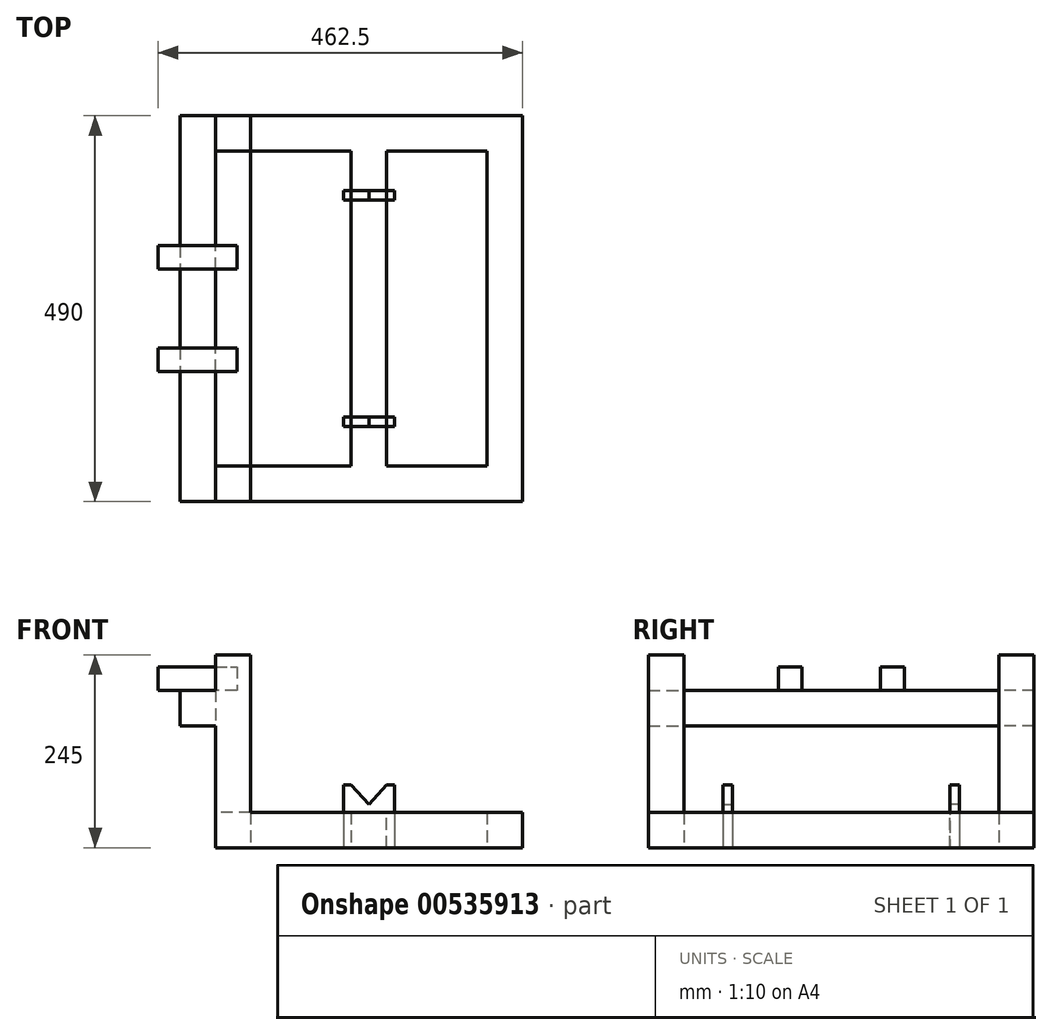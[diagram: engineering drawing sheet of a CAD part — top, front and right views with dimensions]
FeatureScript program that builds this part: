
annotation { "Feature Type Name" : "Feature", "Feature Type Description" : "" }
export const myFeature = defineFeature(function(context is Context, id is Id, definition is map)
    precondition{}
    {
        {
            var Q0;
            Q0=qCreatedBy(makeId("Top.planeOp"),FACE);
            var sketch = newSketch(context, id + "F0", { "sketchPlane" : qUnion([Q0])});
            skLineSegment(sketch, "E0.bottom", {"start": v(0, 0) * mm, "end": v(390, 0) * mm});
            skLineSegment(sketch, "E0.top", {"start": v(0, 490) * mm, "end": v(390, 490) * mm});
            skLineSegment(sketch, "E0.left", {"start": v(0, 0) * mm, "end": v(0, 490) * mm});
            skLineSegment(sketch, "E0.right", {"start": v(390, 0) * mm, "end": v(390, 490) * mm});
            skLineSegment(sketch, "E1.bottom", {"start": v(45, 445) * mm, "end": v(172.5, 445) * mm});
            skLineSegment(sketch, "E1.top", {"start": v(45, 45) * mm, "end": v(172.5, 45) * mm});
            skLineSegment(sketch, "E1.left", {"start": v(45, 445) * mm, "end": v(45, 45) * mm});
            skLineSegment(sketch, "E1.right", {"start": v(345, 445) * mm, "end": v(345, 45) * mm});
            skLineSegment(sketch, "E2", {"start": v(172.5, 445) * mm, "end": v(172.5, 45) * mm});
            skLineSegment(sketch, "E3", {"start": v(217.5, 445) * mm, "end": v(217.5, 45) * mm});
            skLineSegment(sketch, "E4.trimOffspring", {"start": v(217.5, 445) * mm, "end": v(345, 445) * mm});
            skLineSegment(sketch, "E5.trimOffspring", {"start": v(217.5, 45) * mm, "end": v(345, 45) * mm});
            skSolve(sketch);
        }
        {
            var Q0;
            Q0=makeQuery(id+"F0.imprint","IMPRINT",FACE,{"disambiguationData":[TD([[makeQuery(id+"F0.imprint","IMPRINT",EDGE,{"derivedFrom":sQuery(id+"F0.wireOp",EDGE,"E0.bottom")}),1.0]])]});
            extrude(context, id + "F1", {"entities" : qUnion([Q0]), "depth" : 45 * mm, "offsetDistance" : 25 * mm});
        }
        {
            var Q0;
            Q0=makeQuery(id+"F1.opExtrude","CAP_FACE",FACE,{"disambiguationData":[OSD([sQuery(id+"F0.wireOp",EDGE,"E0.bottom"),sQuery(id+"F0.wireOp",EDGE,"E0.top"),sQuery(id+"F0.wireOp",EDGE,"E0.left"),sQuery(id+"F0.wireOp",EDGE,"E0.right"),sQuery(id+"F0.wireOp",EDGE,"E1.bottom"),sQuery(id+"F0.wireOp",EDGE,"E1.top"),sQuery(id+"F0.wireOp",EDGE,"E1.left"),sQuery(id+"F0.wireOp",EDGE,"E1.right"),sQuery(id+"F0.wireOp",EDGE,"E2"),sQuery(id+"F0.wireOp",EDGE,"E3"),sQuery(id+"F0.wireOp",EDGE,"E4.trimOffspring"),sQuery(id+"F0.wireOp",EDGE,"E5.trimOffspring")])],"isStart":false});
            var sketch = newSketch(context, id + "F2", { "sketchPlane" : qUnion([Q0])});
            skLineSegment(sketch, "E6.bottom", {"start": v(45, 445) * mm, "end": v(0, 445) * mm});
            skLineSegment(sketch, "E6.top", {"start": v(45, 490) * mm, "end": v(0, 490) * mm});
            skLineSegment(sketch, "E6.left", {"start": v(45, 445) * mm, "end": v(45, 490) * mm});
            skLineSegment(sketch, "E6.right", {"start": v(0, 445) * mm, "end": v(0, 490) * mm});
            skLineSegment(sketch, "E7.bottom", {"start": v(45, 45) * mm, "end": v(0, 45) * mm});
            skLineSegment(sketch, "E7.top", {"start": v(45, 0) * mm, "end": v(0, 0) * mm});
            skLineSegment(sketch, "E7.left", {"start": v(45, 45) * mm, "end": v(45, 0) * mm});
            skLineSegment(sketch, "E7.right", {"start": v(0, 45) * mm, "end": v(0, 0) * mm});
            skSolve(sketch);
        }
        {
            var Q0;
            Q0=makeQuery(id+"F2.imprint","IMPRINT",FACE,{"disambiguationData":[TD([[makeQuery(id+"F2.imprint","IMPRINT",EDGE,{"derivedFrom":sQuery(id+"F2.wireOp",EDGE,"E7.bottom")}),1.0]])]});
            var Q1;
            Q1=makeQuery(id+"F2.imprint","IMPRINT",FACE,{"disambiguationData":[TD([[makeQuery(id+"F2.imprint","IMPRINT",EDGE,{"derivedFrom":sQuery(id+"F2.wireOp",EDGE,"E6.bottom")}),-1.0]])]});
            extrude(context, id + "F3", {"entities" : qUnion([Q0, Q1]), "operationType" : NewBodyOperationType.ADD, "depth" : 200 * mm, "offsetDistance" : 25 * mm});
        }
        {
            var Q0;
            Q0=makeQuery(id+"F3.boolean.opBoolean","MERGE",FACE,{"derivedFrom":[makeQuery(id+"F1.opExtrude","SWEPT_FACE",FACE,{"disambiguationData":[OSD([sQuery(id+"F0.wireOp",EDGE,"E0.left")])]}),makeQuery(id+"F3.opExtrude","SWEPT_FACE",FACE,{"disambiguationData":[OSD([sQuery(id+"F2.wireOp",EDGE,"E6.right")])]}),makeQuery(id+"F3.opExtrude","SWEPT_FACE",FACE,{"disambiguationData":[OSD([sQuery(id+"F2.wireOp",EDGE,"E7.right")])]})]});
            var sketch = newSketch(context, id + "F4", { "sketchPlane" : qUnion([Q0])});
            skLineSegment(sketch, "E8.bottom", {"start": v(-490, 200) * mm, "end": v(-445, 200) * mm});
            skLineSegment(sketch, "E8.top", {"start": v(-490, 155) * mm, "end": v(-445, 155) * mm});
            skLineSegment(sketch, "E8.left", {"start": v(-490, 200) * mm, "end": v(-490, 155) * mm});
            skLineSegment(sketch, "E8.right", {"start": v(-445, 200) * mm, "end": v(-445, 155) * mm});
            skSolve(sketch);
        }
        {
            var Q0;
            Q0=makeQuery(id+"F4.imprint","IMPRINT",FACE,{"disambiguationData":[TD([[makeQuery(id+"F4.imprint","IMPRINT",EDGE,{"derivedFrom":sQuery(id+"F4.wireOp",EDGE,"E8.bottom")}),-1.0]])]});
            extrude(context, id + "F5", {"entities" : qUnion([Q0]), "operationType" : NewBodyOperationType.ADD, "depth" : 45 * mm, "offsetDistance" : 25 * mm});
        }
        {
            var Q0;
            Q0=makeQuery(id+"F5.boolean.opBoolean","MERGE",FACE,{"derivedFrom":[makeQuery(id+"F3.opExtrude","SWEPT_FACE",FACE,{"disambiguationData":[OSD([sQuery(id+"F2.wireOp",EDGE,"E6.bottom")])]}),makeQuery(id+"F5.opExtrude","SWEPT_FACE",FACE,{"disambiguationData":[OSD([sQuery(id+"F4.wireOp",EDGE,"E8.right")])]})]});
            var sketch = newSketch(context, id + "F6", { "sketchPlane" : qUnion([Q0])});
            skLineSegment(sketch, "E9.bottom", {"start": v(0, 155) * mm, "end": v(-45, 155) * mm});
            skLineSegment(sketch, "E9.top", {"start": v(0, 200) * mm, "end": v(-45, 200) * mm});
            skLineSegment(sketch, "E9.left", {"start": v(0, 155) * mm, "end": v(0, 200) * mm});
            skLineSegment(sketch, "E9.right", {"start": v(-45, 155) * mm, "end": v(-45, 200) * mm});
            skSolve(sketch);
        }
        {
            var Q0;
            Q0=makeQuery(id+"F6.imprint","IMPRINT",FACE,{"disambiguationData":[TD([[makeQuery(id+"F6.imprint","IMPRINT",EDGE,{"derivedFrom":sQuery(id+"F6.wireOp",EDGE,"E9.bottom")}),1.0]])]});
            extrude(context, id + "F7", {"entities" : qUnion([Q0]), "operationType" : NewBodyOperationType.ADD, "depth" : 445 * mm, "offsetDistance" : 25 * mm});
        }
        {
            var Q0;
            Q0=makeQuery(id+"F1.opExtrude","SWEPT_FACE",FACE,{"disambiguationData":[OSD([sQuery(id+"F0.wireOp",EDGE,"E3")])]});
            var sketch = newSketch(context, id + "F8", { "sketchPlane" : qUnion([Q0])});
            skLineSegment(sketch, "E10.bottom", {"start": v(95, 45) * mm, "end": v(107, 45) * mm});
            skLineSegment(sketch, "E10.top", {"start": v(95, 0) * mm, "end": v(107, 0) * mm});
            skLineSegment(sketch, "E10.left", {"start": v(95, 45) * mm, "end": v(95, 0) * mm});
            skLineSegment(sketch, "E10.right", {"start": v(107, 45) * mm, "end": v(107, 0) * mm});
            skSolve(sketch);
        }
        {
            var Q0;
            Q0=makeQuery(id+"F8.imprint","IMPRINT",FACE,{"disambiguationData":[TD([[makeQuery(id+"F8.imprint","IMPRINT",EDGE,{"derivedFrom":sQuery(id+"F8.wireOp",EDGE,"E10.bottom")}),1.0]])]});
            extrude(context, id + "F9", {"entities" : qUnion([Q0]), "operationType" : NewBodyOperationType.ADD, "depth" : 10 * mm, "offsetDistance" : 25 * mm});
        }
        {
            var Q0;
            Q0=makeQuery(id+"F1.opExtrude","SWEPT_FACE",FACE,{"disambiguationData":[OSD([sQuery(id+"F0.wireOp",EDGE,"E2")])]});
            var sketch = newSketch(context, id + "F10", { "sketchPlane" : qUnion([Q0])});
            skLineSegment(sketch, "E11.bottom", {"start": v(-95, 45) * mm, "end": v(-107, 45) * mm});
            skLineSegment(sketch, "E11.top", {"start": v(-95, 0) * mm, "end": v(-107, 0) * mm});
            skLineSegment(sketch, "E11.left", {"start": v(-95, 45) * mm, "end": v(-95, 0) * mm});
            skLineSegment(sketch, "E11.right", {"start": v(-107, 45) * mm, "end": v(-107, 0) * mm});
            skSolve(sketch);
        }
        {
            var Q0;
            Q0=makeQuery(id+"F10.imprint","IMPRINT",FACE,{"disambiguationData":[TD([[makeQuery(id+"F10.imprint","IMPRINT",EDGE,{"derivedFrom":sQuery(id+"F10.wireOp",EDGE,"E11.bottom")}),-1.0]])]});
            extrude(context, id + "F11", {"entities" : qUnion([Q0]), "operationType" : NewBodyOperationType.ADD, "depth" : 10 * mm, "offsetDistance" : 25 * mm});
        }
        {
            var Q0;
            {var subQ0=sQuery(id+"F0.wireOp",EDGE,"E2");var subQ1=sQuery(id+"F0.wireOp",EDGE,"E1.right");var subQ2=sQuery(id+"F0.wireOp",EDGE,"E1.left");var subQ3=sQuery(id+"F0.wireOp",EDGE,"E1.top");var subQ4=sQuery(id+"F0.wireOp",EDGE,"E1.bottom");var subQ5=sQuery(id+"F0.wireOp",EDGE,"E3");var subQ6=sQuery(id+"F0.wireOp",EDGE,"E0.bottom");var subQ7=sQuery(id+"F0.wireOp",EDGE,"E0.right");var subQ8=sQuery(id+"F0.wireOp",EDGE,"E5.trimOffspring");var subQ9=sQuery(id+"F0.wireOp",EDGE,"E4.trimOffspring");var subQ10=sQuery(id+"F0.wireOp",EDGE,"E0.top");var subQ11=makeQuery(id+"F1.opExtrude","CAP_FACE",FACE,{"disambiguationData":[OSD([subQ6,subQ10,sQuery(id+"F0.wireOp",EDGE,"E0.left"),subQ7,subQ4,subQ3,subQ2,subQ1,subQ0,subQ5,subQ9,subQ8])],"isStart":false});Q0=makeQuery(id+"F11.boolean.opBoolean","MERGE",FACE,{"derivedFrom":[makeQuery(id+"F9.boolean.opBoolean","MERGE",FACE,{"derivedFrom":[makeQuery(id+"F3.boolean.opBoolean","SPLIT",FACE,{"disambiguationData":[TD([makeQuery(id+"F1.opExtrude","SWEPT_FACE",FACE,{"disambiguationData":[OSD([subQ6])]})])],"derivedFrom":subQ11}),makeQuery(id+"F9.opExtrude","SWEPT_FACE",FACE,{"disambiguationData":[OSD([sQuery(id+"F8.wireOp",EDGE,"E10.bottom")])]})]}),makeQuery(id+"F11.opExtrude","SWEPT_FACE",FACE,{"disambiguationData":[OSD([sQuery(id+"F10.wireOp",EDGE,"E11.bottom")])]})]});}
            var sketch = newSketch(context, id + "F12", { "sketchPlane" : qUnion([Q0])});
            skLineSegment(sketch, "E12.bottom", {"start": v(227.5, 95) * mm, "end": v(162.5, 95) * mm});
            skLineSegment(sketch, "E12.top", {"start": v(227.5, 107) * mm, "end": v(162.5, 107) * mm});
            skLineSegment(sketch, "E12.left", {"start": v(227.5, 95) * mm, "end": v(227.5, 107) * mm});
            skLineSegment(sketch, "E12.right", {"start": v(162.5, 95) * mm, "end": v(162.5, 107) * mm});
            skSolve(sketch);
        }
        {
            var Q0;
            {var subQ19=sQuery(id+"F12.wireOp",EDGE,"E12.left");Q0=makeQuery(id+"F12.imprint","IMPRINT",FACE,{"disambiguationData":[TD([[makeQuery(id+"F12.imprint","IMPRINT",EDGE,{"derivedFrom":subQ19}),-1.0]])]});}
            extrude(context, id + "F13", {"entities" : qUnion([Q0]), "operationType" : NewBodyOperationType.ADD, "depth" : 35 * mm, "offsetDistance" : 25 * mm});
        }
        {
            var Q0;
            Q0=makeQuery(id+"F13.boolean.opBoolean","MERGE",FACE,{"derivedFrom":[makeQuery(id+"F9.opExtrude","SWEPT_FACE",FACE,{"disambiguationData":[OSD([sQuery(id+"F8.wireOp",EDGE,"E10.right")])]}),makeQuery(id+"F11.opExtrude","SWEPT_FACE",FACE,{"disambiguationData":[OSD([sQuery(id+"F10.wireOp",EDGE,"E11.right")])]}),makeQuery(id+"F13.opExtrude","SWEPT_FACE",FACE,{"disambiguationData":[OSD([sQuery(id+"F12.wireOp",EDGE,"E12.top")])]})]});
            var sketch = newSketch(context, id + "F14", { "sketchPlane" : qUnion([Q0])});
            skLineSegment(sketch, "E13", {"start": v(-217.5, 80) * mm, "end": v(-195, 55) * mm});
            skLineSegment(sketch, "E14", {"start": v(-195, 55) * mm, "end": v(-172.5, 80) * mm});
            skLineSegment(sketch, "E15", {"start": v(-217.5, 80) * mm, "end": v(-172.5, 80) * mm});
            skPoint(sketch, "E16.orphan", {"position": v(-195, 80) * mm});
            skPoint(sketch, "E17.end.orphan", {"position": v(-195, 45) * mm});
            skSolve(sketch);
        }
        {
            var Q0;
            Q0=makeQuery(id+"F14.imprint","IMPRINT",FACE,{"disambiguationData":[TD([[makeQuery(id+"F14.imprint","IMPRINT",EDGE,{"derivedFrom":sQuery(id+"F14.wireOp",EDGE,"E13")}),1.0]])]});
            extrude(context, id + "F15", {"entities" : qUnion([Q0]), "operationType" : NewBodyOperationType.REMOVE, "oppositeDirection" : true, "depth" : 12 * mm, "offsetDistance" : 25 * mm});
        }
        {
            var Q0;
            {var subQ0=sQuery(id+"F0.wireOp",EDGE,"E4.trimOffspring");var subQ2=sQuery(id+"F0.wireOp",EDGE,"E3");Q0=makeQuery(id+"F9.boolean.opBoolean","SPLIT",FACE,{"disambiguationData":[TD([makeQuery(id+"F1.opExtrude","SWEPT_FACE",FACE,{"disambiguationData":[OSD([subQ0])]})])],"derivedFrom":makeQuery(id+"F1.opExtrude","SWEPT_FACE",FACE,{"disambiguationData":[OSD([subQ2])]})});}
            var sketch = newSketch(context, id + "F16", { "sketchPlane" : qUnion([Q0])});
            skLineSegment(sketch, "E18.bottom", {"start": v(395, 0) * mm, "end": v(383, 0) * mm});
            skLineSegment(sketch, "E18.top", {"start": v(395, 45) * mm, "end": v(383, 45) * mm});
            skLineSegment(sketch, "E18.left", {"start": v(395, 0) * mm, "end": v(395, 45) * mm});
            skLineSegment(sketch, "E18.right", {"start": v(383, 0) * mm, "end": v(383, 45) * mm});
            skSolve(sketch);
        }
        {
            var Q0;
            Q0=makeQuery(id+"F16.imprint","IMPRINT",FACE,{"disambiguationData":[TD([[makeQuery(id+"F16.imprint","IMPRINT",EDGE,{"derivedFrom":sQuery(id+"F16.wireOp",EDGE,"E18.bottom")}),-1.0]])]});
            extrude(context, id + "F17", {"entities" : qUnion([Q0]), "operationType" : NewBodyOperationType.ADD, "depth" : 10 * mm, "offsetDistance" : 25 * mm});
        }
        {
            var Q0;
            {var subQ3=sQuery(id+"F0.wireOp",EDGE,"E2");var subQ7=sQuery(id+"F0.wireOp",EDGE,"E1.bottom");Q0=makeQuery(id+"F11.boolean.opBoolean","SPLIT",FACE,{"disambiguationData":[TD([makeQuery(id+"F1.opExtrude","SWEPT_FACE",FACE,{"disambiguationData":[OSD([subQ7])]})])],"derivedFrom":makeQuery(id+"F1.opExtrude","SWEPT_FACE",FACE,{"disambiguationData":[OSD([subQ3])]})});}
            var sketch = newSketch(context, id + "F18", { "sketchPlane" : qUnion([Q0])});
            skLineSegment(sketch, "E19.bottom", {"start": v(-395, 45) * mm, "end": v(-383, 45) * mm});
            skLineSegment(sketch, "E19.top", {"start": v(-395, 0) * mm, "end": v(-383, 0) * mm});
            skLineSegment(sketch, "E19.left", {"start": v(-395, 45) * mm, "end": v(-395, 0) * mm});
            skLineSegment(sketch, "E19.right", {"start": v(-383, 45) * mm, "end": v(-383, 0) * mm});
            skSolve(sketch);
        }
        {
            var Q0;
            Q0=makeQuery(id+"F18.imprint","IMPRINT",FACE,{"disambiguationData":[TD([[makeQuery(id+"F18.imprint","IMPRINT",EDGE,{"derivedFrom":sQuery(id+"F18.wireOp",EDGE,"E19.bottom")}),-1.0]])]});
            extrude(context, id + "F19", {"entities" : qUnion([Q0]), "operationType" : NewBodyOperationType.ADD, "depth" : 10 * mm, "offsetDistance" : 25 * mm});
        }
        {
            var Q0;
            {var subQ0=sQuery(id+"F0.wireOp",EDGE,"E2");var subQ1=sQuery(id+"F0.wireOp",EDGE,"E1.right");var subQ2=sQuery(id+"F0.wireOp",EDGE,"E1.left");var subQ3=sQuery(id+"F0.wireOp",EDGE,"E1.top");var subQ4=sQuery(id+"F0.wireOp",EDGE,"E1.bottom");var subQ5=sQuery(id+"F0.wireOp",EDGE,"E3");var subQ6=sQuery(id+"F0.wireOp",EDGE,"E0.bottom");var subQ7=sQuery(id+"F0.wireOp",EDGE,"E0.right");var subQ8=sQuery(id+"F0.wireOp",EDGE,"E5.trimOffspring");var subQ9=sQuery(id+"F0.wireOp",EDGE,"E4.trimOffspring");var subQ10=sQuery(id+"F0.wireOp",EDGE,"E0.top");var subQ11=makeQuery(id+"F1.opExtrude","CAP_FACE",FACE,{"disambiguationData":[OSD([subQ6,subQ10,sQuery(id+"F0.wireOp",EDGE,"E0.left"),subQ7,subQ4,subQ3,subQ2,subQ1,subQ0,subQ5,subQ9,subQ8])],"isStart":false});Q0=makeQuery(id+"F19.boolean.opBoolean","MERGE",FACE,{"derivedFrom":[makeQuery(id+"F17.boolean.opBoolean","MERGE",FACE,{"derivedFrom":[makeQuery(id+"F11.boolean.opBoolean","MERGE",FACE,{"derivedFrom":[makeQuery(id+"F9.boolean.opBoolean","MERGE",FACE,{"derivedFrom":[makeQuery(id+"F3.boolean.opBoolean","SPLIT",FACE,{"disambiguationData":[TD([makeQuery(id+"F1.opExtrude","SWEPT_FACE",FACE,{"disambiguationData":[OSD([subQ6])]})])],"derivedFrom":subQ11}),makeQuery(id+"F9.opExtrude","SWEPT_FACE",FACE,{"disambiguationData":[OSD([sQuery(id+"F8.wireOp",EDGE,"E10.bottom")])]})]}),makeQuery(id+"F11.opExtrude","SWEPT_FACE",FACE,{"disambiguationData":[OSD([sQuery(id+"F10.wireOp",EDGE,"E11.bottom")])]})]}),makeQuery(id+"F17.opExtrude","SWEPT_FACE",FACE,{"disambiguationData":[OSD([sQuery(id+"F16.wireOp",EDGE,"E18.top")])]})]}),makeQuery(id+"F19.opExtrude","SWEPT_FACE",FACE,{"disambiguationData":[OSD([sQuery(id+"F18.wireOp",EDGE,"E19.bottom")])]})]});}
            var sketch = newSketch(context, id + "F20", { "sketchPlane" : qUnion([Q0])});
            skLineSegment(sketch, "E20.bottom", {"start": v(227.5, 395) * mm, "end": v(162.5, 395) * mm});
            skLineSegment(sketch, "E20.top", {"start": v(227.5, 383) * mm, "end": v(162.5, 383) * mm});
            skLineSegment(sketch, "E20.left", {"start": v(227.5, 395) * mm, "end": v(227.5, 383) * mm});
            skLineSegment(sketch, "E20.right", {"start": v(162.5, 395) * mm, "end": v(162.5, 383) * mm});
            skSolve(sketch);
        }
        {
            var Q0;
            {var subQ24=sQuery(id+"F20.wireOp",EDGE,"E20.left");Q0=makeQuery(id+"F20.imprint","IMPRINT",FACE,{"disambiguationData":[TD([[makeQuery(id+"F20.imprint","IMPRINT",EDGE,{"derivedFrom":subQ24}),-1.0]])]});}
            extrude(context, id + "F21", {"entities" : qUnion([Q0]), "operationType" : NewBodyOperationType.ADD, "depth" : 35 * mm, "offsetDistance" : 25 * mm});
        }
        {
            var Q0;
            Q0=makeQuery(id+"F21.boolean.opBoolean","MERGE",FACE,{"derivedFrom":[makeQuery(id+"F17.opExtrude","SWEPT_FACE",FACE,{"disambiguationData":[OSD([sQuery(id+"F16.wireOp",EDGE,"E18.right")])]}),makeQuery(id+"F19.opExtrude","SWEPT_FACE",FACE,{"disambiguationData":[OSD([sQuery(id+"F18.wireOp",EDGE,"E19.right")])]}),makeQuery(id+"F21.opExtrude","SWEPT_FACE",FACE,{"disambiguationData":[OSD([sQuery(id+"F20.wireOp",EDGE,"E20.top")])]})]});
            var sketch = newSketch(context, id + "F22", { "sketchPlane" : qUnion([Q0])});
            skLineSegment(sketch, "E21", {"start": v(172.5, 80) * mm, "end": v(195, 55) * mm});
            skLineSegment(sketch, "E22", {"start": v(195, 55) * mm, "end": v(217.5, 80) * mm});
            skLineSegment(sketch, "E23", {"start": v(172.5, 80) * mm, "end": v(217.5, 80) * mm});
            skPoint(sketch, "E24.orphan", {"position": v(195, 80) * mm});
            skPoint(sketch, "E25.end.orphan", {"position": v(195, 45) * mm});
            skSolve(sketch);
        }
        {
            var Q0;
            Q0=makeQuery(id+"F22.imprint","IMPRINT",FACE,{"disambiguationData":[TD([[makeQuery(id+"F22.imprint","IMPRINT",EDGE,{"derivedFrom":sQuery(id+"F22.wireOp",EDGE,"E21")}),1.0]])]});
            extrude(context, id + "F23", {"entities" : qUnion([Q0]), "operationType" : NewBodyOperationType.REMOVE, "oppositeDirection" : true, "depth" : 12 * mm, "offsetDistance" : 25 * mm});
        }
        {
            var Q0;
            Q0=makeQuery(id+"F7.boolean.opBoolean","MERGE",FACE,{"derivedFrom":[makeQuery(id+"F5.opExtrude","SWEPT_FACE",FACE,{"disambiguationData":[OSD([sQuery(id+"F4.wireOp",EDGE,"E8.bottom")])]}),makeQuery(id+"F7.opExtrude","SWEPT_FACE",FACE,{"disambiguationData":[OSD([sQuery(id+"F6.wireOp",EDGE,"E9.top")])]})]});
            var sketch = newSketch(context, id + "F24", { "sketchPlane" : qUnion([Q0])});
            skLineSegment(sketch, "E26", {"start": v(-45, 245) * mm, "end": v(15.63, 245) * mm});
            skPoint(sketch, "E26.endSnap0", {"position": v(0, 245) * mm});
            skLineSegment(sketch, "E27.bottom", {"start": v(-45, 195) * mm, "end": v(0, 195) * mm});
            skLineSegment(sketch, "E27.top", {"start": v(-45, 165) * mm, "end": v(0, 165) * mm});
            skLineSegment(sketch, "E27.left", {"start": v(-45, 195) * mm, "end": v(-45, 165) * mm});
            skLineSegment(sketch, "E27.right", {"start": v(0, 195) * mm, "end": v(0, 165) * mm});
            skLineSegment(sketch, "E28.bottom", {"start": v(-45, 295) * mm, "end": v(0, 295) * mm});
            skLineSegment(sketch, "E28.top", {"start": v(-45, 325) * mm, "end": v(0, 325) * mm});
            skLineSegment(sketch, "E28.left", {"start": v(-45, 295) * mm, "end": v(-45, 325) * mm});
            skLineSegment(sketch, "E28.right", {"start": v(0, 295) * mm, "end": v(0, 325) * mm});
            skSolve(sketch);
        }
        {
            var Q0;
            Q0=makeQuery(id+"F24.imprint","IMPRINT",FACE,{"disambiguationData":[TD([[makeQuery(id+"F24.imprint","IMPRINT",EDGE,{"derivedFrom":sQuery(id+"F24.wireOp",EDGE,"E27.bottom")}),-1.0]])]});
            var Q1;
            Q1=makeQuery(id+"F24.imprint","IMPRINT",FACE,{"disambiguationData":[TD([[makeQuery(id+"F24.imprint","IMPRINT",EDGE,{"derivedFrom":sQuery(id+"F24.wireOp",EDGE,"E28.bottom")}),1.0]])]});
            extrude(context, id + "F25", {"entities" : qUnion([Q0, Q1]), "operationType" : NewBodyOperationType.ADD, "depth" : 30 * mm, "offsetDistance" : 25 * mm});
        }
        {
            var Q0;
            Q0=makeQuery(id+"F25.boolean.opBoolean","MERGE",FACE,{"derivedFrom":[makeQuery(id+"F7.opExtrude","SWEPT_FACE",FACE,{"disambiguationData":[OSD([sQuery(id+"F6.wireOp",EDGE,"E9.left")])]}),makeQuery(id+"F25.opExtrude","SWEPT_FACE",FACE,{"disambiguationData":[OSD([sQuery(id+"F24.wireOp",EDGE,"E27.right")])]}),makeQuery(id+"F25.opExtrude","SWEPT_FACE",FACE,{"disambiguationData":[OSD([sQuery(id+"F24.wireOp",EDGE,"E28.right")])]})]});
            var sketch = newSketch(context, id + "F26", { "sketchPlane" : qUnion([Q0])});
            skLineSegment(sketch, "E29.bottom", {"start": v(165, 230) * mm, "end": v(195, 230) * mm});
            skLineSegment(sketch, "E29.top", {"start": v(165, 200) * mm, "end": v(195, 200) * mm});
            skLineSegment(sketch, "E29.left", {"start": v(165, 230) * mm, "end": v(165, 200) * mm});
            skLineSegment(sketch, "E29.right", {"start": v(195, 230) * mm, "end": v(195, 200) * mm});
            skLineSegment(sketch, "E30.bottom", {"start": v(295, 230) * mm, "end": v(325, 230) * mm});
            skLineSegment(sketch, "E30.top", {"start": v(295, 200) * mm, "end": v(325, 200) * mm});
            skLineSegment(sketch, "E30.left", {"start": v(295, 230) * mm, "end": v(295, 200) * mm});
            skLineSegment(sketch, "E30.right", {"start": v(325, 230) * mm, "end": v(325, 200) * mm});
            skSolve(sketch);
        }
        {
            var Q0;
            Q0=makeQuery(id+"F26.imprint","IMPRINT",FACE,{"disambiguationData":[TD([[makeQuery(id+"F26.imprint","IMPRINT",EDGE,{"derivedFrom":sQuery(id+"F26.wireOp",EDGE,"E30.bottom")}),-1.0]])]});
            var Q1;
            Q1=makeQuery(id+"F26.imprint","IMPRINT",FACE,{"disambiguationData":[TD([[makeQuery(id+"F26.imprint","IMPRINT",EDGE,{"derivedFrom":sQuery(id+"F26.wireOp",EDGE,"E29.bottom")}),-1.0]])]});
            extrude(context, id + "F27", {"entities" : qUnion([Q0, Q1]), "operationType" : NewBodyOperationType.ADD, "depth" : 27.5 * mm, "offsetDistance" : 25 * mm});
        }
        {
            var Q0;
            Q0=makeQuery(id+"F25.boolean.opBoolean","MERGE",FACE,{"derivedFrom":[makeQuery(id+"F7.boolean.opBoolean","MERGE",FACE,{"derivedFrom":[makeQuery(id+"F5.opExtrude","CAP_FACE",FACE,{"disambiguationData":[OSD([sQuery(id+"F4.wireOp",EDGE,"E8.bottom"),sQuery(id+"F4.wireOp",EDGE,"E8.top"),sQuery(id+"F4.wireOp",EDGE,"E8.left"),sQuery(id+"F4.wireOp",EDGE,"E8.right")])],"isStart":false}),makeQuery(id+"F7.opExtrude","SWEPT_FACE",FACE,{"disambiguationData":[OSD([sQuery(id+"F6.wireOp",EDGE,"E9.right")])]})]}),makeQuery(id+"F25.opExtrude","SWEPT_FACE",FACE,{"disambiguationData":[OSD([sQuery(id+"F24.wireOp",EDGE,"E27.left")])]}),makeQuery(id+"F25.opExtrude","SWEPT_FACE",FACE,{"disambiguationData":[OSD([sQuery(id+"F24.wireOp",EDGE,"E28.left")])]})]});
            var sketch = newSketch(context, id + "F28", { "sketchPlane" : qUnion([Q0])});
            skLineSegment(sketch, "E31.bottom", {"start": v(-325, 230) * mm, "end": v(-295, 230) * mm});
            skLineSegment(sketch, "E31.top", {"start": v(-325, 200) * mm, "end": v(-295, 200) * mm});
            skLineSegment(sketch, "E31.left", {"start": v(-325, 230) * mm, "end": v(-325, 200) * mm});
            skLineSegment(sketch, "E31.right", {"start": v(-295, 230) * mm, "end": v(-295, 200) * mm});
            skLineSegment(sketch, "E32.bottom", {"start": v(-195, 230) * mm, "end": v(-165, 230) * mm});
            skLineSegment(sketch, "E32.top", {"start": v(-195, 200) * mm, "end": v(-165, 200) * mm});
            skLineSegment(sketch, "E32.left", {"start": v(-195, 230) * mm, "end": v(-195, 200) * mm});
            skLineSegment(sketch, "E32.right", {"start": v(-165, 230) * mm, "end": v(-165, 200) * mm});
            skSolve(sketch);
        }
        {
            var Q0;
            Q0 = qSketchRegion(id + "F28", true);
            extrude(context, id + "F29", {"entities" : qUnion([Q0]), "operationType" : NewBodyOperationType.ADD, "depth" : 27.5 * mm, "offsetDistance" : 25 * mm});
        }
    });
